# Revit family: Shower-Handshower-KOHLER-Flipside-K-17493_1
name_source: partatom
category: Plumbing Fixtures
revit_build: Autodesk Revit 2015 (Build: 20140606_1530(x64)
units: mm (PartAtom-declared; Revit-internal decimal feet)

## types (4) — shared parameters
ADA Compliant = No
Assembly Code = D2010700
CW Connection = No
Cold Water Inlet = Cold Water Inlet
Date Modified = 11/14/2018
Default Elevation = 0"
Description = 2.5 gpm multifunction handshower
Flow Rate = 3 GPM
HW Connection = Yes
Height = 10 3/4"
Hot Water Inlet = Tempered Water Inlet
Length = 4"
Manufacturer = KOHLER Co.
MasterFormat 1995 = 15410
MasterFormat 2004 = 22.41.23
Material = Premium Metal Construction
Product Documentation Link = http://www.us.kohler.com
Product Name = Flipside
Product Page URL = http://www.us.kohler.com
URL = https://www.us.kohler.com
Vent Connection = No
Waste Connection = No
Waste Water Outlet = Waste Water Outlet
Width = 5 3/8"

## per-type parameters (varying)
| type | Finish | Model | Type |
| CP-Polished Chrome | Kohler-Metal-CP-Polished_Chrome | K-17493-CP | 1 |
| SN-Vibrant Polished Nickel | Kohler-Metal-SN-Vibrant_Polished_Nickel | K-17493-SN | 2 |
| BN-Vibrant  Brushed Nickel | Kohler-Metal-BN-Vibrant_Brushed_Nickel | K-17493-BN | 3 |
| 2BZ-Oil-Rubbed Bronze | Kohler-Metal-2BZ-Oil_Rubbed_Bronze | K-17493-2BZ | 4 |

## geometry (parser evidence)
native form markers: Sweep x2
no freeform markers — native parametric forms only
